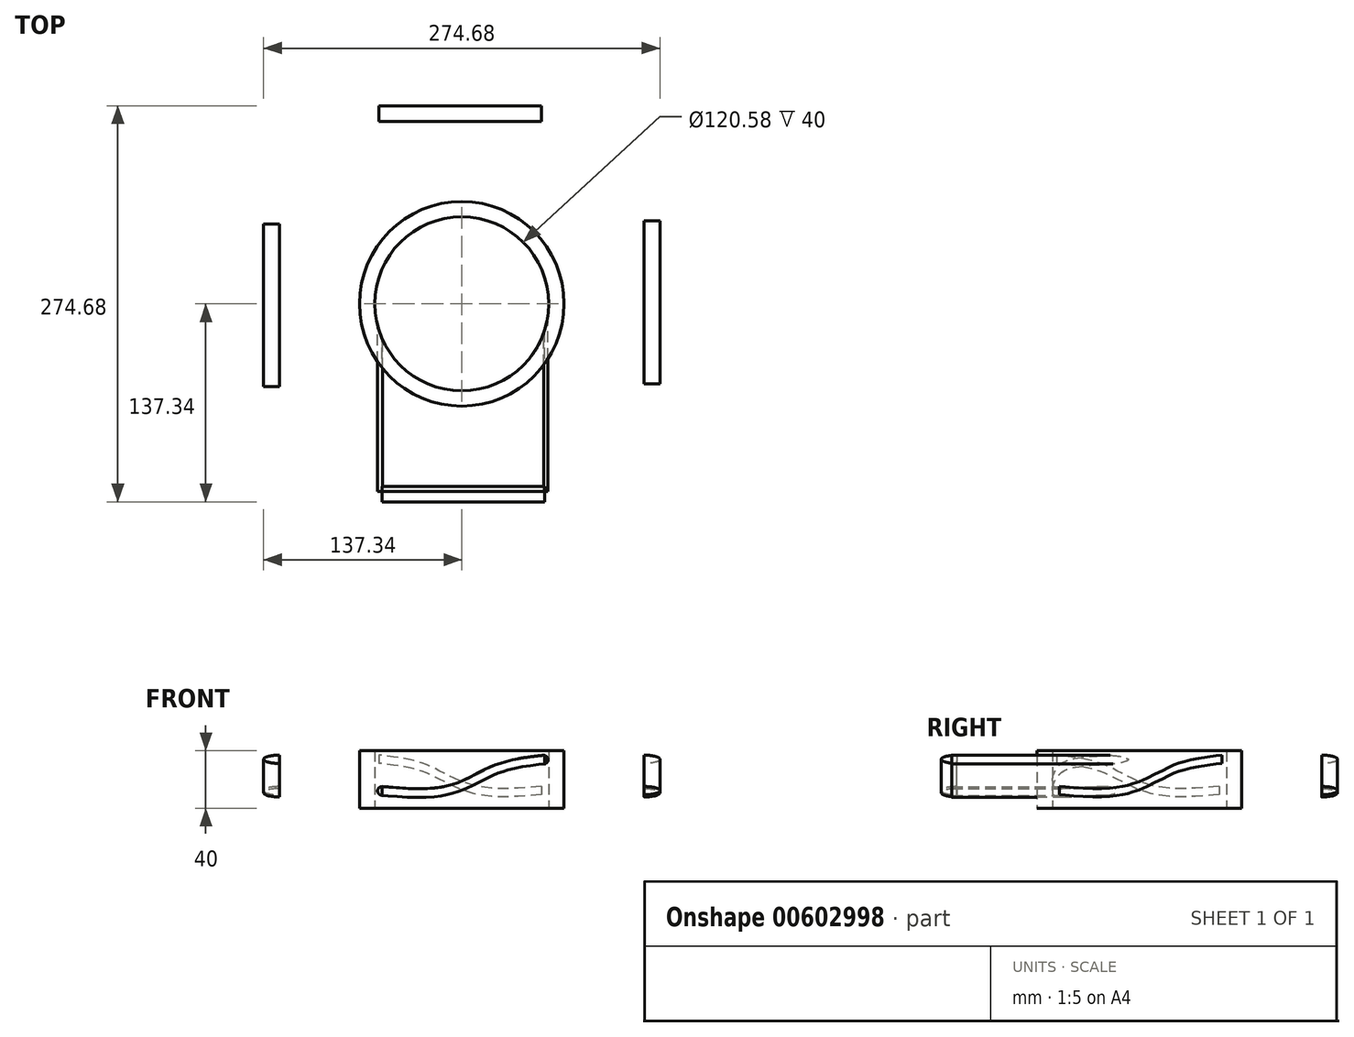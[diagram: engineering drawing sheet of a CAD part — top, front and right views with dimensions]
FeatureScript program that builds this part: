
annotation { "Feature Type Name" : "Feature", "Feature Type Description" : "" }
export const myFeature = defineFeature(function(context is Context, id is Id, definition is map)
    precondition{}
    {
        {
            var Q0;
            Q0=qCreatedBy(makeId("Top.planeOp"),FACE);
            var sketch = newSketch(context, id + "F0", { "sketchPlane" : qUnion([Q0])});
            skCircle(sketch, "E0", {"center": v(0, 0) * mm, "radius": 70.9 * mm});
            skCircle(sketch, "E1", {"center": v(0, 0) * mm, "radius": 60.29 * mm});
            skSolve(sketch);
        }
        {
            var Q0;
            Q0=makeQuery(id+"F0.imprint","IMPRINT",FACE,{"disambiguationData":[TD([[makeQuery(id+"F0.imprint","IMPRINT",EDGE,{"derivedFrom":sQuery(id+"F0.wireOp",EDGE,"E0")}),1.0]])]});
            extrude(context, id + "F1", {"entities" : qUnion([Q0]), "depth" : 40 * mm, "offsetDistance" : 25 * mm});
        }
        {
            var Q0;
            Q0=qCreatedBy(makeId("Front.planeOp"),FACE);
            var sketch = newSketch(context, id + "F2", { "sketchPlane" : qUnion([Q0])});
            skFitSpline(sketch, "E2", {"points": [v(50.14, 37.39) * mm, v(6.12, 27.38) * mm, v(-49.98, 6.83) * mm, v(-31.64, 7.3) * mm, v(14.93, 23.67) * mm, v(45.08, 29.33) * mm, v(64.33, 33.88) * mm, v(50.14, 37.39) * mm]});
            skSolve(sketch);
        }
        {
            var Q0;
            Q0=sQuery(id+"F2.wireOp",EDGE,"E2");
            extrude(context, id + "F3", {"bodyType" : ToolBodyType.SURFACE, "surfaceEntities" : qUnion([Q0]), "depth" : 100 * mm, "offsetDistance" : 25 * mm});
        }
        {
            var Q0;
            Q0=qCreatedBy(makeId("Front.planeOp"),FACE);
            var sketch = newSketch(context, id + "F4", { "sketchPlane" : qUnion([Q0])});
            skFitSpline(sketch, "E3", {"points": [v(57.08, 33.78) * mm, v(24.63, 27.37) * mm, v(-8.2, 13) * mm, v(-55.13, 12.06) * mm], "startDerivative": vector(-107.19, -11.95) * mm, "endDerivative": vector(-134.74, 11.07) * mm});
            skFitSpline(sketch, "E4.0", {"points": [v(56.75, 36.76) * mm, v(54.52, 36.51) * mm, v(50.03, 36.01) * mm, v(43.27, 35.12) * mm, v(37.65, 34.14) * mm, v(33.18, 33.14) * mm, v(29.84, 32.27) * mm, v(27.07, 31.42) * mm, v(24.88, 30.67) * mm, v(22.69, 29.85) * mm, v(20, 28.73) * mm, v(16.83, 27.27) * mm, v(13.7, 25.74) * mm, v(9.58, 23.65) * mm, v(5.48, 21.57) * mm, v(1.34, 19.63) * mm, v(-1.8, 18.29) * mm, v(-5, 17.09) * mm, v(-7.73, 16.23) * mm, v(-9.94, 15.65) * mm, v(-12.21, 15.13) * mm, v(-15.12, 14.6) * mm, v(-18.74, 14.14) * mm, v(-23.7, 13.73) * mm, v(-30.16, 13.57) * mm, v(-38.2, 13.82) * mm, v(-46.47, 14.36) * mm, v(-52.07, 14.82) * mm, v(-54.88, 15.05) * mm]});
            skFitSpline(sketch, "E5.0", {"points": [v(57.41, 30.8) * mm, v(55.18, 30.55) * mm, v(50.73, 30.05) * mm, v(44.16, 29.18) * mm, v(38.8, 28.25) * mm, v(34.58, 27.3) * mm, v(31.47, 26.5) * mm, v(28.92, 25.71) * mm, v(26.9, 25.02) * mm, v(24.9, 24.27) * mm, v(22.42, 23.24) * mm, v(19.42, 21.86) * mm, v(16.4, 20.38) * mm, v(12.32, 18.31) * mm, v(7.1, 15.66) * mm, v(1.6, 13.16) * mm, v(-3.04, 11.42) * mm, v(-6.04, 10.47) * mm, v(-8.52, 9.82) * mm, v(-11.02, 9.25) * mm, v(-14.21, 8.67) * mm, v(-18.12, 8.17) * mm, v(-23.42, 7.73) * mm, v(-30.2, 7.57) * mm, v(-38.52, 7.82) * mm, v(-46.93, 8.37) * mm, v(-52.56, 8.84) * mm, v(-55.37, 9.07) * mm]});
            skArc(sketch, "E6", {"start": v(-54.88, 15.05) * mm, "mid": v(-58.34, 12.32) * mm, "end": v(-55.37, 9.07) * mm});
            skArc(sketch, "E7", {"start": v(57.41, 30.8) * mm, "mid": v(59.78, 34.08) * mm, "end": v(56.75, 36.76) * mm});
            skSolve(sketch);
        }
        {
            var Q0;
            Q0 = qSketchRegion(id + "F4", true);
            extrude(context, id + "F5", {"entities" : qUnion([Q0]), "depth" : 130 * mm, "offsetDistance" : 25 * mm});
        }
        {
            var Q0;
            Q0=qCreatedBy(makeId("Right.planeOp"),FACE);
            var sketch = newSketch(context, id + "F6", { "sketchPlane" : qUnion([Q0])});
            skEllipticalArc(sketch, "E8", {});
            skLineSegment(sketch, "E9", {"start": v(-119.17, 36.76) * mm, "end": v(-119.17, 31.04) * mm});
            const initialGuessF6  = {"E8": [-0.11916622519493103, 0.03389998525381088, -1, 0, 0.010881930589675903, 0.0028587149976163737, 4.71238898038469, 1.5707963267948966]};
            skSetInitialGuess(sketch, initialGuessF6);
            skSolve(sketch);
        }
        {
            var Q0;
            Q0=makeQuery(id+"F6.imprint","IMPRINT",FACE,{"disambiguationData":[TD([[makeQuery(id+"F6.imprint","IMPRINT",EDGE,{"derivedFrom":sQuery(id+"F6.wireOp",EDGE,"E8")}),1.0]])]});
            var Q1;
            Q1=makeQuery(id+"F5.opExtrude","CAP_EDGE",EDGE,{"disambiguationData":[OSD([sQuery(id+"F4.wireOp",EDGE,"E5.0")])],"isStart":false});
            sweep(context, id + "F7", {"profiles" : qUnion([Q0]), "path" : qUnion([Q1]), "keepProfileOrientation" : true});
        }
        {
            var Q0;
            Q0=makeQuery(id+"F7.opSweep","SWEPT_BODY",BODY,{"disambiguationData":[OSD([sQuery(id+"F4.wireOp",EDGE,"E5.0"),sQuery(id+"F6.wireOp",EDGE,"E8"),sQuery(id+"F6.wireOp",EDGE,"E9")])]});
            transform(context, id + "F8", {"entities" : qUnion([Q0]), "transformType" : TransformType.TRANSLATION_3D, "dx" : 0 * mm, "dy" : -17.01 * mm, "dz" : -19.12 * mm, "makeCopy" : false});
        }
        {
            var Q0;
            Q0=makeQuery(id+"F0.imprint","IMPRINT",FACE,{"disambiguationData":[TD([[makeQuery(id+"F0.imprint","IMPRINT",EDGE,{"derivedFrom":sQuery(id+"F0.wireOp",EDGE,"E1")}),1.0]])]});
            var Q1;
            Q1=sQuery(id+"F0.wireOp",EDGE,"E1");
            extrude(context, id + "F9", {"entities" : qUnion([Q0]), "operationType" : NewBodyOperationType.REMOVE, "surfaceEntities" : qUnion([Q1]), "depth" : 60 * mm, "offsetDistance" : 25 * mm});
        }
        {
            var Q0;
            Q0=makeQuery(id+"F7.opSweep","SWEPT_BODY",BODY,{"disambiguationData":[OSD([sQuery(id+"F4.wireOp",EDGE,"E5.0"),sQuery(id+"F6.wireOp",EDGE,"E8"),sQuery(id+"F6.wireOp",EDGE,"E9")])]});
            transform(context, id + "F10", {"entities" : qUnion([Q0]), "transformType" : TransformType.TRANSLATION_3D, "dx" : 0 * mm, "dy" : 9.72 * mm, "dz" : 0 * mm, "makeCopy" : false});
        }
        {
            var Q0;
            Q0=makeQuery(id+"F7.opSweep","SWEPT_BODY",BODY,{"disambiguationData":[OSD([sQuery(id+"F4.wireOp",EDGE,"E5.0"),sQuery(id+"F6.wireOp",EDGE,"E8"),sQuery(id+"F6.wireOp",EDGE,"E9")])]});
            transform(context, id + "F11", {"entities" : qUnion([Q0]), "transformType" : TransformType.TRANSLATION_3D, "dx" : 0 * mm, "dy" : 0 * mm, "dz" : 1 * mm, "makeCopy" : false});
        }
        {
            var Q0;
            Q0=makeQuery(id+"F7.opSweep","SWEPT_BODY",BODY,{"disambiguationData":[OSD([sQuery(id+"F4.wireOp",EDGE,"E5.0"),sQuery(id+"F6.wireOp",EDGE,"E8"),sQuery(id+"F6.wireOp",EDGE,"E9")])]});
            var Q1;
            Q1=makeQuery(id+"F1.opExtrude","CAP_EDGE",EDGE,{"disambiguationData":[OSD([sQuery(id+"F0.wireOp",EDGE,"E0")])],"isStart":false});
            circularPattern(context, id + "F12", {"entities" : qUnion([Q0]), "axis" : qUnion([Q1]), "angle" : 360 * degree, "instanceCount" : 4, "equalSpace" : true});
        }
    });
